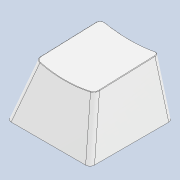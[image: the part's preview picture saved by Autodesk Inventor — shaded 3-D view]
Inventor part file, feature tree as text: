
AUTODESK INVENTOR PART (.ipt)
format: ipt  version: 2021 (Build 250183000, 183)  size: 251,904 bytes
history: native  units: in
note: dims shown in document units (in); Inventor stores cm internally (conversion verified against a paired STEP export)
features: chamfer x1
ambient origin geometry x8: Origin, YZ Plane, XZ Plane, XY Plane, X Axis, Y Axis, Z Axis, Center Point
bodies: Solid1 (feature_tree)
feature tree (1):
  chamfer  "Chamfer1"  [1 undecoded]
note: 1 required parameter value undecoded (feature->parameter linkage not recoverable at this tier; creation-order binding heuristic only, values carry confidence <= 0.55)
